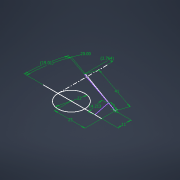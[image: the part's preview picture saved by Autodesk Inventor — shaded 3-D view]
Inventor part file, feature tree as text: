
AUTODESK INVENTOR PART (.ipt)
format: ipt  version: 2021 (Build 250183000, 183)  size: 90,624 bytes
history: native  units: mm
features: sketch x1
ambient origin geometry x8: Origin, YZ Plane, XZ Plane, XY Plane, X Axis, Y Axis, Z Axis, Center Point
feature tree (1):
  sketch  "Sketch1"  dims[d1=9.0mm d3=0.0mm d4=11.0mm d6=22.0mm d7=25.0mm d9=3.490659mm d11=3.317786mm d13=41.0mm d14=2.764mm d15=14.2127mm]
